# Revit family: QF_BOURGEAT_Satellite4G_GN80_chaud_2-1_porte_vitree
name_source: partatom
category: Equipement spécialisé
revit_build: Autodesk Revit 2015 (Build: 20140606_1530(x64)
units: mm (PartAtom-declared; Revit-internal decimal feet)

## types (2) — shared parameters
Certification = NF hygiene alimentaire
Charge max = 290.00 kg
Consommation énergétique = 2.96Kwh/h NFD40-016
Diametre_roue = 160 mm  [stored 0.524934 ft]
Fabricant = BOURGEAT
Fréquence = 50 Hz
Hauteur hors tout = 1917 mm  [stored 6.28937 ft]
Hauteur_poignee_porte_sol = 767 mm  [stored 2.5164 ft]
Hauteur_poignees_laterales = 905 mm  [stored 2.96916 ft]
Hauteur_porte = 1626 mm  [stored 5.33465 ft]
Hauteur_roue = 200 mm  [stored 0.656168 ft]
Indice de protection = IP25
Intensité nominale = 15 A
Largeur_porte = 703 mm  [stored 2.30643 ft]
Longueur hors tout = 1616 mm  [stored 5.30184 ft]
Longueur_poignees_laterales = 759 mm  [stored 2.49016 ft]
Materiau_Poignee_porte = B_Elastomère_TPE_S
Materiau_bac = B_Elastomère_TPE_S
Materiau_bandage = B_Elastomère_TPE_S
Materiau_porte = Acier inoxydable, brossé
Materiau_vitre = Verre, vitrage transparent, trempé
Nature isolant = Mousse sans PU
Phase = 2
Poids net à vide = 400.00 kg
Poignee_droite = Non
Poignee_gauche = Oui
Pos_V_IHM = 197 mm
Profondeur hors tout = 959 mm  [stored 3.14633 ft]
Puissance électrique  = 3500 W
Spécification du Fabricant = Satellite 4G
Tension = 230 V
URL catalogue = http://www.bourgeat.fr

## per-type parameters (varying)
| type | Humidification | Modèle |
| GN80_humidification_porte_vitree | Oui | 841380 |
| GN80_sans_humidification_porte_vitree | Non | 841280 |

note: [stored X ft] marks values corroborated as IEEE doubles in the binary element streams (Revit-internal decimal feet)
